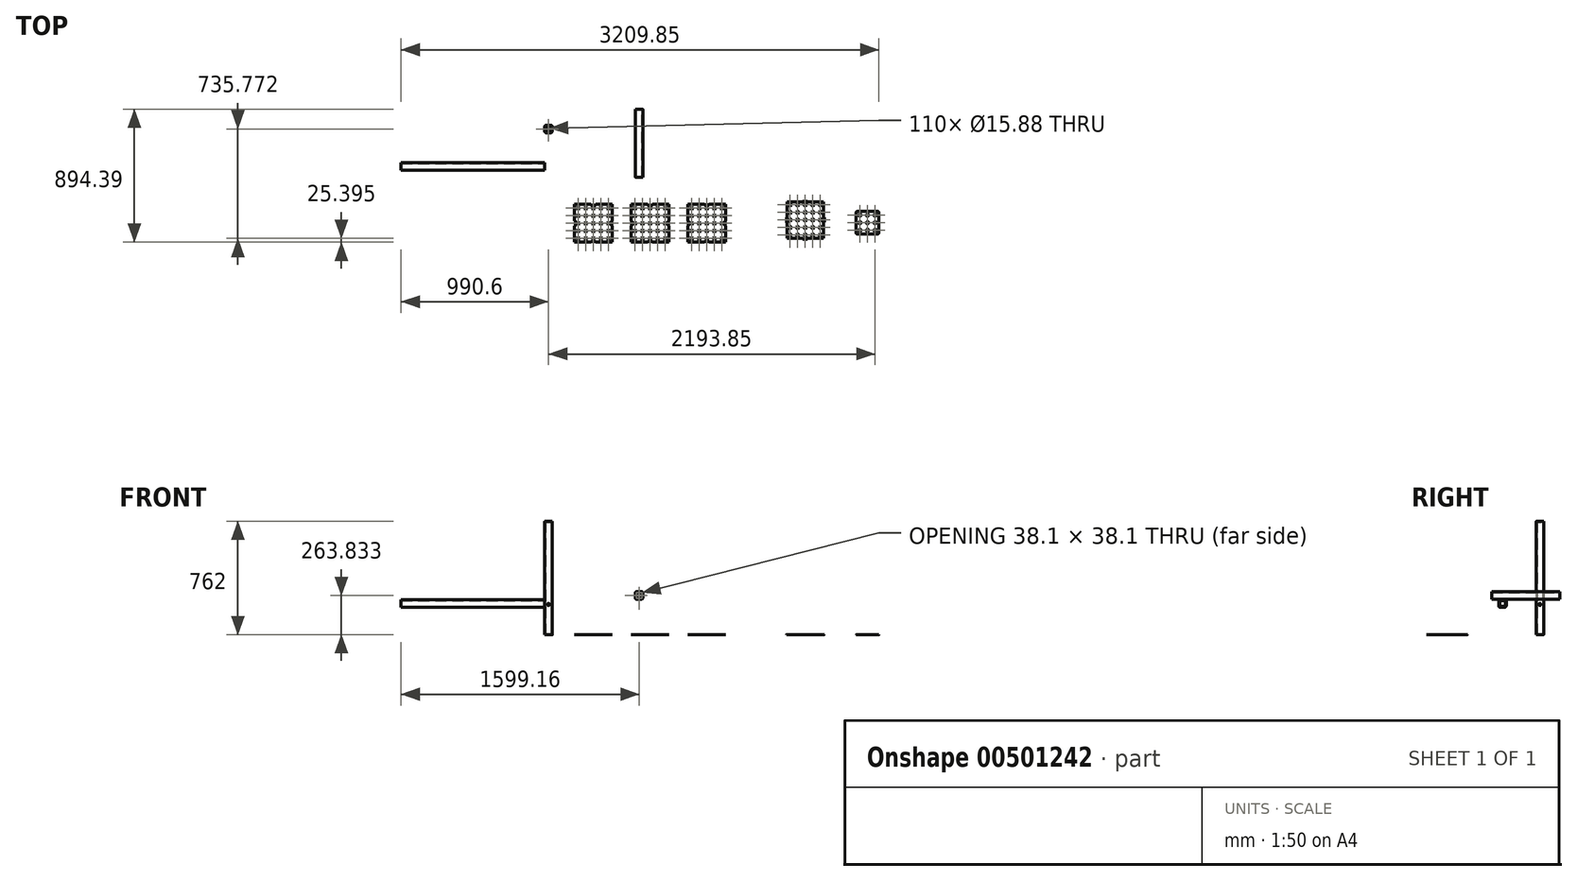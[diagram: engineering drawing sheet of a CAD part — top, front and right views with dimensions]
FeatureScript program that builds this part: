
annotation { "Feature Type Name" : "Feature", "Feature Type Description" : "" }
export const myFeature = defineFeature(function(context is Context, id is Id, definition is map)
    precondition{}
    {
        {
            assignVariable(context, id + "F0", {"name" : "TopPlateThickness", "anyValue" : 0.25});
        }
        {
            assignVariable(context, id + "F1", {"name" : "CornerPlateThickness", "anyValue" : 0.25});
        }
        {
            var Q0;
            Q0=qCreatedBy(makeId("Top.planeOp"),FACE);
            var sketch = newSketch(context, id + "F2", { "sketchPlane" : qUnion([Q0])});
            skLineSegment(sketch, "E0.bottom", {"start": v(-372.68, -640.4) * mm, "end": v(-118.68, -640.4) * mm});
            skLineSegment(sketch, "E0.top", {"start": v(-372.68, -894.4) * mm, "end": v(-118.68, -894.4) * mm});
            skLineSegment(sketch, "E0.left", {"start": v(-372.68, -640.4) * mm, "end": v(-372.68, -894.4) * mm});
            skLineSegment(sketch, "E0.right", {"start": v(-118.68, -640.4) * mm, "end": v(-118.68, -894.4) * mm});
            skLineSegment(sketch, "E1", {"start": v(-372.68, -665.8) * mm, "end": v(-347.28, -665.8) * mm, "construction": true});
            skLineSegment(sketch, "E2", {"start": v(-347.28, -665.8) * mm, "end": v(-347.28, -640.4) * mm, "construction": true});
            skCircle(sketch, "E3", {"center": v(-347.28, -665.8) * mm, "radius": 7.94 * mm});
            skCircle(sketch, "E4.0.1.0", {"center": v(-347.28, -716.6) * mm, "radius": 7.94 * mm});
            skCircle(sketch, "E4.0.2.0", {"center": v(-347.28, -767.4) * mm, "radius": 7.94 * mm});
            skCircle(sketch, "E4.0.3.0", {"center": v(-347.28, -818.2) * mm, "radius": 7.94 * mm});
            skCircle(sketch, "E4.1.0.0", {"center": v(-296.48, -665.8) * mm, "radius": 7.94 * mm});
            skCircle(sketch, "E4.1.1.0", {"center": v(-296.48, -716.6) * mm, "radius": 7.94 * mm});
            skCircle(sketch, "E4.1.2.0", {"center": v(-296.48, -767.4) * mm, "radius": 7.94 * mm});
            skCircle(sketch, "E4.1.3.0", {"center": v(-296.48, -818.2) * mm, "radius": 7.94 * mm});
            skCircle(sketch, "E4.2.0.0", {"center": v(-245.68, -665.8) * mm, "radius": 7.94 * mm});
            skCircle(sketch, "E4.2.1.0", {"center": v(-245.68, -716.6) * mm, "radius": 7.94 * mm});
            skCircle(sketch, "E4.2.2.0", {"center": v(-245.68, -767.4) * mm, "radius": 7.94 * mm});
            skCircle(sketch, "E4.2.3.0", {"center": v(-245.68, -818.2) * mm, "radius": 7.94 * mm});
            skCircle(sketch, "E4.3.0.0", {"center": v(-194.88, -665.8) * mm, "radius": 7.94 * mm});
            skCircle(sketch, "E4.3.1.0", {"center": v(-194.88, -716.6) * mm, "radius": 7.94 * mm});
            skCircle(sketch, "E4.3.2.0", {"center": v(-194.88, -767.4) * mm, "radius": 7.94 * mm});
            skCircle(sketch, "E4.3.3.0", {"center": v(-194.88, -818.2) * mm, "radius": 7.94 * mm});
            skCircle(sketch, "E4.4.0.0", {"center": v(-144.08, -665.8) * mm, "radius": 7.94 * mm});
            skCircle(sketch, "E4.4.1.0", {"center": v(-144.08, -716.6) * mm, "radius": 7.94 * mm});
            skCircle(sketch, "E4.4.2.0", {"center": v(-144.08, -767.4) * mm, "radius": 7.94 * mm});
            skCircle(sketch, "E4.4.3.0", {"center": v(-144.08, -818.2) * mm, "radius": 7.94 * mm});
            skLineSegment(sketch, "E4.direction1", {"start": v(-347.28, -665.8) * mm, "end": v(-296.48, -665.8) * mm, "construction": true});
            skLineSegment(sketch, "E4.direction2", {"start": v(-347.28, -665.8) * mm, "end": v(-347.28, -716.6) * mm, "construction": true});
            skLineSegment(sketch, "E5.MirrorCS", {"start": v(138.85, -74.13) * mm, "end": v(138.95, -80.47) * mm});
            skLineSegment(sketch, "E6", {"start": v(170.72, -73.61) * mm, "end": v(170.82, -79.96) * mm});
            skArc(sketch, "E7", {"start": v(141.8, -73.28) * mm, "mid": v(140, -72.57) * mm, "end": v(138.85, -74.13) * mm});
            skArc(sketch, "E8", {"start": v(141.8, -73.28) * mm, "mid": v(142.39, -73.86) * mm, "end": v(143.18, -74.06) * mm});
            skArc(sketch, "E9.MirrorCS", {"start": v(167.75, -72.87) * mm, "mid": v(169.52, -72.1) * mm, "end": v(170.72, -73.61) * mm});
            skArc(sketch, "E10.MirrorCS", {"start": v(167.75, -72.87) * mm, "mid": v(167.17, -73.46) * mm, "end": v(166.38, -73.68) * mm});
            skLineSegment(sketch, "E11.trimOffspring", {"start": v(166.38, -73.68) * mm, "end": v(143.18, -74.06) * mm});
            skLineSegment(sketch, "E12", {"start": v(138.85, -74.13) * mm, "end": v(143.18, -74.06) * mm, "construction": true});
            skLineSegment(sketch, "E13", {"start": v(166.38, -73.68) * mm, "end": v(170.72, -73.61) * mm, "construction": true});
            skLineSegment(sketch, "E14", {"start": v(154.78, -73.87) * mm, "end": v(154.89, -80.22) * mm, "construction": true});
            skLineSegment(sketch, "E15", {"start": v(138.95, -80.47) * mm, "end": v(154.89, -80.22) * mm, "construction": true});
            skLineSegment(sketch, "E16.MirrorCS", {"start": v(-261.62, -891.22) * mm, "end": v(-261.62, -894.4) * mm});
            skLineSegment(sketch, "E17", {"start": v(-229.74, -891.22) * mm, "end": v(-229.74, -894.4) * mm});
            skArc(sketch, "E18", {"start": v(-258.66, -890.43) * mm, "mid": v(-260.44, -889.69) * mm, "end": v(-261.62, -891.22) * mm});
            skArc(sketch, "E19", {"start": v(-258.66, -890.43) * mm, "mid": v(-258.08, -891) * mm, "end": v(-257.28, -891.22) * mm});
            skArc(sketch, "E20.MirrorCS", {"start": v(-232.7, -890.43) * mm, "mid": v(-230.92, -889.69) * mm, "end": v(-229.74, -891.22) * mm});
            skArc(sketch, "E21.MirrorCS", {"start": v(-232.7, -890.43) * mm, "mid": v(-233.29, -891) * mm, "end": v(-234.08, -891.22) * mm});
            skLineSegment(sketch, "E22.trimOffspring", {"start": v(-234.08, -891.22) * mm, "end": v(-257.28, -891.22) * mm});
            skLineSegment(sketch, "E23", {"start": v(-261.62, -891.22) * mm, "end": v(-257.28, -891.22) * mm, "construction": true});
            skLineSegment(sketch, "E24", {"start": v(-234.08, -891.22) * mm, "end": v(-229.74, -891.22) * mm, "construction": true});
            skLineSegment(sketch, "E25", {"start": v(-245.68, -891.22) * mm, "end": v(-245.68, -894.4) * mm, "construction": true});
            skLineSegment(sketch, "E26", {"start": v(-261.62, -894.4) * mm, "end": v(-245.68, -894.4) * mm, "construction": true});
            skLineSegment(sketch, "E27.MirrorCS", {"start": v(-366.33, -751.46) * mm, "end": v(-372.68, -751.46) * mm});
            skLineSegment(sketch, "E28", {"start": v(-366.33, -783.33) * mm, "end": v(-372.68, -783.33) * mm});
            skArc(sketch, "E29", {"start": v(-365.54, -754.42) * mm, "mid": v(-364.8, -752.63) * mm, "end": v(-366.33, -751.46) * mm});
            skArc(sketch, "E30", {"start": v(-365.54, -754.42) * mm, "mid": v(-366.12, -755) * mm, "end": v(-366.33, -755.8) * mm});
            skArc(sketch, "E31.MirrorCS", {"start": v(-365.54, -780.37) * mm, "mid": v(-364.8, -782.16) * mm, "end": v(-366.33, -783.33) * mm});
            skArc(sketch, "E32.MirrorCS", {"start": v(-365.54, -780.37) * mm, "mid": v(-366.12, -779.79) * mm, "end": v(-366.33, -779) * mm});
            skLineSegment(sketch, "E33.trimOffspring", {"start": v(-366.33, -779) * mm, "end": v(-366.33, -755.8) * mm});
            skLineSegment(sketch, "E34", {"start": v(-366.33, -751.46) * mm, "end": v(-366.33, -755.8) * mm, "construction": true});
            skLineSegment(sketch, "E35", {"start": v(-366.33, -779) * mm, "end": v(-366.33, -783.33) * mm, "construction": true});
            skLineSegment(sketch, "E36", {"start": v(-366.33, -767.4) * mm, "end": v(-372.68, -767.4) * mm, "construction": true});
            skLineSegment(sketch, "E37", {"start": v(-372.68, -751.46) * mm, "end": v(-372.68, -767.4) * mm, "construction": true});
            skCircle(sketch, "E38.0.0.4", {"center": v(-347.28, -869) * mm, "radius": 7.94 * mm});
            skCircle(sketch, "E38.0.1.4", {"center": v(-296.48, -869) * mm, "radius": 7.94 * mm});
            skCircle(sketch, "E38.0.2.4", {"center": v(-245.68, -869) * mm, "radius": 7.94 * mm});
            skCircle(sketch, "E38.0.3.4", {"center": v(-194.88, -869) * mm, "radius": 7.94 * mm});
            skCircle(sketch, "E38.0.4.4", {"center": v(-144.08, -869) * mm, "radius": 7.94 * mm});
            skLineSegment(sketch, "E39.MirrorCS", {"start": v(-121.86, -783.33) * mm, "end": v(-118.68, -783.33) * mm});
            skLineSegment(sketch, "E40", {"start": v(-121.86, -751.46) * mm, "end": v(-118.68, -751.46) * mm});
            skArc(sketch, "E41", {"start": v(-122.65, -780.37) * mm, "mid": v(-123.39, -782.16) * mm, "end": v(-121.86, -783.33) * mm});
            skArc(sketch, "E42", {"start": v(-122.65, -780.37) * mm, "mid": v(-122.07, -779.79) * mm, "end": v(-121.86, -779) * mm});
            skArc(sketch, "E43.MirrorCS", {"start": v(-122.65, -754.42) * mm, "mid": v(-123.39, -752.63) * mm, "end": v(-121.86, -751.46) * mm});
            skArc(sketch, "E44.MirrorCS", {"start": v(-122.65, -754.42) * mm, "mid": v(-122.07, -755) * mm, "end": v(-121.86, -755.8) * mm});
            skLineSegment(sketch, "E45.trimOffspring", {"start": v(-121.86, -755.8) * mm, "end": v(-121.86, -779) * mm});
            skLineSegment(sketch, "E46", {"start": v(-121.86, -783.33) * mm, "end": v(-121.86, -779) * mm, "construction": true});
            skLineSegment(sketch, "E47", {"start": v(-121.86, -755.8) * mm, "end": v(-121.86, -751.46) * mm, "construction": true});
            skLineSegment(sketch, "E48", {"start": v(-121.86, -767.4) * mm, "end": v(-118.68, -767.4) * mm, "construction": true});
            skLineSegment(sketch, "E49", {"start": v(-118.68, -783.33) * mm, "end": v(-118.68, -767.4) * mm, "construction": true});
            skLineSegment(sketch, "E50.MirrorCS", {"start": v(-229.74, -646.74) * mm, "end": v(-229.74, -640.4) * mm});
            skLineSegment(sketch, "E51", {"start": v(-261.62, -646.74) * mm, "end": v(-261.62, -640.4) * mm});
            skArc(sketch, "E52", {"start": v(-232.7, -647.54) * mm, "mid": v(-230.92, -648.28) * mm, "end": v(-229.74, -646.74) * mm});
            skArc(sketch, "E53", {"start": v(-232.7, -647.54) * mm, "mid": v(-233.29, -646.96) * mm, "end": v(-234.08, -646.74) * mm});
            skArc(sketch, "E54.MirrorCS", {"start": v(-258.66, -647.54) * mm, "mid": v(-260.44, -648.28) * mm, "end": v(-261.62, -646.74) * mm});
            skArc(sketch, "E55.MirrorCS", {"start": v(-258.66, -647.54) * mm, "mid": v(-258.08, -646.96) * mm, "end": v(-257.28, -646.74) * mm});
            skLineSegment(sketch, "E56.trimOffspring", {"start": v(-257.28, -646.74) * mm, "end": v(-234.08, -646.74) * mm});
            skLineSegment(sketch, "E57", {"start": v(-229.74, -646.74) * mm, "end": v(-234.08, -646.74) * mm, "construction": true});
            skLineSegment(sketch, "E58", {"start": v(-257.28, -646.74) * mm, "end": v(-261.62, -646.74) * mm, "construction": true});
            skLineSegment(sketch, "E59", {"start": v(-245.68, -646.74) * mm, "end": v(-245.68, -640.4) * mm, "construction": true});
            skLineSegment(sketch, "E60", {"start": v(-229.74, -640.4) * mm, "end": v(-245.68, -640.4) * mm, "construction": true});
            skLineSegment(sketch, "E61.bottom", {"start": v(8.32, -640.4) * mm, "end": v(262.32, -640.4) * mm});
            skLineSegment(sketch, "E61.top", {"start": v(8.32, -894.4) * mm, "end": v(262.32, -894.4) * mm});
            skLineSegment(sketch, "E61.left", {"start": v(8.32, -640.4) * mm, "end": v(8.32, -894.4) * mm});
            skLineSegment(sketch, "E61.right", {"start": v(262.32, -640.4) * mm, "end": v(262.32, -894.4) * mm});
            skLineSegment(sketch, "E62", {"start": v(8.32, -665.8) * mm, "end": v(33.72, -665.8) * mm, "construction": true});
            skLineSegment(sketch, "E63", {"start": v(33.72, -665.8) * mm, "end": v(33.72, -640.4) * mm, "construction": true});
            skCircle(sketch, "E64", {"center": v(33.72, -665.8) * mm, "radius": 7.94 * mm});
            skCircle(sketch, "E65.0.1.0", {"center": v(33.72, -716.6) * mm, "radius": 7.94 * mm});
            skCircle(sketch, "E65.0.2.0", {"center": v(33.72, -767.4) * mm, "radius": 7.94 * mm});
            skCircle(sketch, "E65.0.3.0", {"center": v(33.72, -818.2) * mm, "radius": 7.94 * mm});
            skCircle(sketch, "E65.1.0.0", {"center": v(84.52, -665.8) * mm, "radius": 7.94 * mm});
            skCircle(sketch, "E65.1.1.0", {"center": v(84.52, -716.6) * mm, "radius": 7.94 * mm});
            skCircle(sketch, "E65.1.2.0", {"center": v(84.52, -767.4) * mm, "radius": 7.94 * mm});
            skCircle(sketch, "E65.1.3.0", {"center": v(84.52, -818.2) * mm, "radius": 7.94 * mm});
            skCircle(sketch, "E65.2.0.0", {"center": v(135.32, -665.8) * mm, "radius": 7.94 * mm});
            skCircle(sketch, "E65.2.1.0", {"center": v(135.32, -716.6) * mm, "radius": 7.94 * mm});
            skCircle(sketch, "E65.2.2.0", {"center": v(135.32, -767.4) * mm, "radius": 7.94 * mm});
            skCircle(sketch, "E65.2.3.0", {"center": v(135.32, -818.2) * mm, "radius": 7.94 * mm});
            skCircle(sketch, "E65.3.0.0", {"center": v(186.12, -665.8) * mm, "radius": 7.94 * mm});
            skCircle(sketch, "E65.3.1.0", {"center": v(186.12, -716.6) * mm, "radius": 7.94 * mm});
            skCircle(sketch, "E65.3.2.0", {"center": v(186.12, -767.4) * mm, "radius": 7.94 * mm});
            skCircle(sketch, "E65.3.3.0", {"center": v(186.12, -818.2) * mm, "radius": 7.94 * mm});
            skCircle(sketch, "E65.4.0.0", {"center": v(236.92, -665.8) * mm, "radius": 7.94 * mm});
            skCircle(sketch, "E65.4.1.0", {"center": v(236.92, -716.6) * mm, "radius": 7.94 * mm});
            skCircle(sketch, "E65.4.2.0", {"center": v(236.92, -767.4) * mm, "radius": 7.94 * mm});
            skCircle(sketch, "E65.4.3.0", {"center": v(236.92, -818.2) * mm, "radius": 7.94 * mm});
            skLineSegment(sketch, "E65.direction1", {"start": v(33.72, -665.8) * mm, "end": v(84.52, -665.8) * mm, "construction": true});
            skLineSegment(sketch, "E65.direction2", {"start": v(33.72, -665.8) * mm, "end": v(33.72, -716.6) * mm, "construction": true});
            skLineSegment(sketch, "E66.MirrorCS", {"start": v(119.38, -891.22) * mm, "end": v(119.38, -894.4) * mm});
            skLineSegment(sketch, "E67", {"start": v(151.26, -891.22) * mm, "end": v(151.26, -894.4) * mm});
            skArc(sketch, "E68", {"start": v(122.34, -890.43) * mm, "mid": v(120.56, -889.69) * mm, "end": v(119.38, -891.22) * mm});
            skArc(sketch, "E69", {"start": v(122.34, -890.43) * mm, "mid": v(122.92, -891) * mm, "end": v(123.72, -891.22) * mm});
            skArc(sketch, "E70.MirrorCS", {"start": v(148.3, -890.43) * mm, "mid": v(150.08, -889.69) * mm, "end": v(151.26, -891.22) * mm});
            skArc(sketch, "E71.MirrorCS", {"start": v(148.3, -890.43) * mm, "mid": v(147.71, -891) * mm, "end": v(146.92, -891.22) * mm});
            skLineSegment(sketch, "E72.trimOffspring", {"start": v(146.92, -891.22) * mm, "end": v(123.72, -891.22) * mm});
            skLineSegment(sketch, "E73", {"start": v(119.38, -891.22) * mm, "end": v(123.72, -891.22) * mm, "construction": true});
            skLineSegment(sketch, "E74", {"start": v(146.92, -891.22) * mm, "end": v(151.26, -891.22) * mm, "construction": true});
            skLineSegment(sketch, "E75", {"start": v(135.32, -891.22) * mm, "end": v(135.32, -894.4) * mm, "construction": true});
            skLineSegment(sketch, "E76", {"start": v(119.38, -894.4) * mm, "end": v(135.32, -894.4) * mm, "construction": true});
            skLineSegment(sketch, "E77.MirrorCS", {"start": v(11.5, -751.46) * mm, "end": v(8.32, -751.46) * mm});
            skLineSegment(sketch, "E78", {"start": v(11.5, -783.33) * mm, "end": v(8.32, -783.33) * mm});
            skArc(sketch, "E79", {"start": v(12.29, -754.42) * mm, "mid": v(13.03, -752.63) * mm, "end": v(11.5, -751.46) * mm});
            skArc(sketch, "E80", {"start": v(12.29, -754.42) * mm, "mid": v(11.7, -755) * mm, "end": v(11.5, -755.8) * mm});
            skArc(sketch, "E81.MirrorCS", {"start": v(12.29, -780.37) * mm, "mid": v(13.03, -782.16) * mm, "end": v(11.5, -783.33) * mm});
            skArc(sketch, "E82.MirrorCS", {"start": v(12.29, -780.37) * mm, "mid": v(11.7, -779.79) * mm, "end": v(11.5, -779) * mm});
            skLineSegment(sketch, "E83.trimOffspring", {"start": v(11.5, -779) * mm, "end": v(11.5, -755.8) * mm});
            skLineSegment(sketch, "E84", {"start": v(11.5, -751.46) * mm, "end": v(11.5, -755.8) * mm, "construction": true});
            skLineSegment(sketch, "E85", {"start": v(11.5, -779) * mm, "end": v(11.5, -783.33) * mm, "construction": true});
            skLineSegment(sketch, "E86", {"start": v(11.5, -767.4) * mm, "end": v(8.32, -767.4) * mm, "construction": true});
            skLineSegment(sketch, "E87", {"start": v(8.32, -751.46) * mm, "end": v(8.32, -767.4) * mm, "construction": true});
            skCircle(sketch, "E88.0.0.4", {"center": v(33.72, -869) * mm, "radius": 7.94 * mm});
            skCircle(sketch, "E88.0.1.4", {"center": v(84.52, -869) * mm, "radius": 7.94 * mm});
            skCircle(sketch, "E88.0.2.4", {"center": v(135.32, -869) * mm, "radius": 7.94 * mm});
            skCircle(sketch, "E88.0.3.4", {"center": v(186.12, -869) * mm, "radius": 7.94 * mm});
            skCircle(sketch, "E88.0.4.4", {"center": v(236.92, -869) * mm, "radius": 7.94 * mm});
            skLineSegment(sketch, "E89.MirrorCS", {"start": v(259.14, -783.33) * mm, "end": v(262.32, -783.33) * mm});
            skLineSegment(sketch, "E90", {"start": v(259.14, -751.46) * mm, "end": v(262.32, -751.46) * mm});
            skArc(sketch, "E91", {"start": v(258.35, -780.37) * mm, "mid": v(257.61, -782.16) * mm, "end": v(259.14, -783.33) * mm});
            skArc(sketch, "E92", {"start": v(258.35, -780.37) * mm, "mid": v(258.93, -779.79) * mm, "end": v(259.14, -779) * mm});
            skArc(sketch, "E93.MirrorCS", {"start": v(258.35, -754.42) * mm, "mid": v(257.61, -752.63) * mm, "end": v(259.14, -751.46) * mm});
            skArc(sketch, "E94.MirrorCS", {"start": v(258.35, -754.42) * mm, "mid": v(258.93, -755) * mm, "end": v(259.14, -755.8) * mm});
            skLineSegment(sketch, "E95.trimOffspring", {"start": v(259.14, -755.8) * mm, "end": v(259.14, -779) * mm});
            skLineSegment(sketch, "E96", {"start": v(259.14, -783.33) * mm, "end": v(259.14, -779) * mm, "construction": true});
            skLineSegment(sketch, "E97", {"start": v(259.14, -755.8) * mm, "end": v(259.14, -751.46) * mm, "construction": true});
            skLineSegment(sketch, "E98", {"start": v(259.14, -767.4) * mm, "end": v(262.32, -767.4) * mm, "construction": true});
            skLineSegment(sketch, "E99", {"start": v(262.32, -783.33) * mm, "end": v(262.32, -767.4) * mm, "construction": true});
            skLineSegment(sketch, "E100.MirrorCS", {"start": v(151.26, -646.74) * mm, "end": v(151.26, -640.4) * mm});
            skLineSegment(sketch, "E101", {"start": v(119.38, -646.74) * mm, "end": v(119.38, -640.4) * mm});
            skArc(sketch, "E102", {"start": v(148.3, -647.54) * mm, "mid": v(150.08, -648.28) * mm, "end": v(151.26, -646.74) * mm});
            skArc(sketch, "E103", {"start": v(148.3, -647.54) * mm, "mid": v(147.71, -646.96) * mm, "end": v(146.92, -646.74) * mm});
            skArc(sketch, "E104.MirrorCS", {"start": v(122.34, -647.54) * mm, "mid": v(120.56, -648.28) * mm, "end": v(119.38, -646.74) * mm});
            skArc(sketch, "E105.MirrorCS", {"start": v(122.34, -647.54) * mm, "mid": v(122.92, -646.96) * mm, "end": v(123.72, -646.74) * mm});
            skLineSegment(sketch, "E106.trimOffspring", {"start": v(123.72, -646.74) * mm, "end": v(146.92, -646.74) * mm});
            skLineSegment(sketch, "E107", {"start": v(151.26, -646.74) * mm, "end": v(146.92, -646.74) * mm, "construction": true});
            skLineSegment(sketch, "E108", {"start": v(123.72, -646.74) * mm, "end": v(119.38, -646.74) * mm, "construction": true});
            skLineSegment(sketch, "E109", {"start": v(135.32, -646.74) * mm, "end": v(135.32, -640.4) * mm, "construction": true});
            skLineSegment(sketch, "E110", {"start": v(151.26, -640.4) * mm, "end": v(135.32, -640.4) * mm, "construction": true});
            skLineSegment(sketch, "E111.bottom", {"start": v(389.32, -640.4) * mm, "end": v(643.32, -640.4) * mm});
            skLineSegment(sketch, "E111.top", {"start": v(389.32, -894.4) * mm, "end": v(643.32, -894.4) * mm});
            skLineSegment(sketch, "E111.left", {"start": v(389.32, -640.4) * mm, "end": v(389.32, -894.4) * mm});
            skLineSegment(sketch, "E111.right", {"start": v(643.32, -640.4) * mm, "end": v(643.32, -894.4) * mm});
            skLineSegment(sketch, "E112", {"start": v(389.32, -665.8) * mm, "end": v(414.72, -665.8) * mm, "construction": true});
            skLineSegment(sketch, "E113", {"start": v(414.72, -665.8) * mm, "end": v(414.72, -640.4) * mm, "construction": true});
            skCircle(sketch, "E114", {"center": v(414.72, -665.8) * mm, "radius": 7.94 * mm});
            skCircle(sketch, "E115.0.1.0", {"center": v(414.72, -716.6) * mm, "radius": 7.94 * mm});
            skCircle(sketch, "E115.0.2.0", {"center": v(414.72, -767.4) * mm, "radius": 7.94 * mm});
            skCircle(sketch, "E115.0.3.0", {"center": v(414.72, -818.2) * mm, "radius": 7.94 * mm});
            skCircle(sketch, "E115.1.0.0", {"center": v(465.52, -665.8) * mm, "radius": 7.94 * mm});
            skCircle(sketch, "E115.1.1.0", {"center": v(465.52, -716.6) * mm, "radius": 7.94 * mm});
            skCircle(sketch, "E115.1.2.0", {"center": v(465.52, -767.4) * mm, "radius": 7.94 * mm});
            skCircle(sketch, "E115.1.3.0", {"center": v(465.52, -818.2) * mm, "radius": 7.94 * mm});
            skCircle(sketch, "E115.2.0.0", {"center": v(516.32, -665.8) * mm, "radius": 7.94 * mm});
            skCircle(sketch, "E115.2.1.0", {"center": v(516.32, -716.6) * mm, "radius": 7.94 * mm});
            skCircle(sketch, "E115.2.2.0", {"center": v(516.32, -767.4) * mm, "radius": 7.94 * mm});
            skCircle(sketch, "E115.2.3.0", {"center": v(516.32, -818.2) * mm, "radius": 7.94 * mm});
            skCircle(sketch, "E115.3.0.0", {"center": v(567.12, -665.8) * mm, "radius": 7.94 * mm});
            skCircle(sketch, "E115.3.1.0", {"center": v(567.12, -716.6) * mm, "radius": 7.94 * mm});
            skCircle(sketch, "E115.3.2.0", {"center": v(567.12, -767.4) * mm, "radius": 7.94 * mm});
            skCircle(sketch, "E115.3.3.0", {"center": v(567.12, -818.2) * mm, "radius": 7.94 * mm});
            skCircle(sketch, "E115.4.0.0", {"center": v(617.92, -665.8) * mm, "radius": 7.94 * mm});
            skCircle(sketch, "E115.4.1.0", {"center": v(617.92, -716.6) * mm, "radius": 7.94 * mm});
            skCircle(sketch, "E115.4.2.0", {"center": v(617.92, -767.4) * mm, "radius": 7.94 * mm});
            skCircle(sketch, "E115.4.3.0", {"center": v(617.92, -818.2) * mm, "radius": 7.94 * mm});
            skLineSegment(sketch, "E115.direction1", {"start": v(414.72, -665.8) * mm, "end": v(465.52, -665.8) * mm, "construction": true});
            skLineSegment(sketch, "E115.direction2", {"start": v(414.72, -665.8) * mm, "end": v(414.72, -716.6) * mm, "construction": true});
            skLineSegment(sketch, "E116.MirrorCS", {"start": v(500.38, -891.22) * mm, "end": v(500.38, -894.4) * mm});
            skLineSegment(sketch, "E117", {"start": v(532.26, -891.22) * mm, "end": v(532.26, -894.4) * mm});
            skArc(sketch, "E118", {"start": v(503.34, -890.43) * mm, "mid": v(501.56, -889.69) * mm, "end": v(500.38, -891.22) * mm});
            skArc(sketch, "E119", {"start": v(503.34, -890.43) * mm, "mid": v(503.92, -891) * mm, "end": v(504.72, -891.22) * mm});
            skArc(sketch, "E120.MirrorCS", {"start": v(529.3, -890.43) * mm, "mid": v(531.08, -889.69) * mm, "end": v(532.26, -891.22) * mm});
            skArc(sketch, "E121.MirrorCS", {"start": v(529.3, -890.43) * mm, "mid": v(528.71, -891) * mm, "end": v(527.92, -891.22) * mm});
            skLineSegment(sketch, "E122.trimOffspring", {"start": v(527.92, -891.22) * mm, "end": v(504.72, -891.22) * mm});
            skLineSegment(sketch, "E123", {"start": v(500.38, -891.22) * mm, "end": v(504.72, -891.22) * mm, "construction": true});
            skLineSegment(sketch, "E124", {"start": v(527.92, -891.22) * mm, "end": v(532.26, -891.22) * mm, "construction": true});
            skLineSegment(sketch, "E125", {"start": v(516.32, -891.22) * mm, "end": v(516.32, -894.4) * mm, "construction": true});
            skLineSegment(sketch, "E126", {"start": v(500.38, -894.4) * mm, "end": v(516.32, -894.4) * mm, "construction": true});
            skLineSegment(sketch, "E127.MirrorCS", {"start": v(392.5, -751.46) * mm, "end": v(389.32, -751.46) * mm});
            skLineSegment(sketch, "E128", {"start": v(392.5, -783.33) * mm, "end": v(389.32, -783.33) * mm});
            skArc(sketch, "E129", {"start": v(393.29, -754.42) * mm, "mid": v(394.03, -752.63) * mm, "end": v(392.5, -751.46) * mm});
            skArc(sketch, "E130", {"start": v(393.29, -754.42) * mm, "mid": v(392.7, -755) * mm, "end": v(392.5, -755.8) * mm});
            skArc(sketch, "E131.MirrorCS", {"start": v(393.29, -780.37) * mm, "mid": v(394.03, -782.16) * mm, "end": v(392.5, -783.33) * mm});
            skArc(sketch, "E132.MirrorCS", {"start": v(393.29, -780.37) * mm, "mid": v(392.7, -779.79) * mm, "end": v(392.5, -779) * mm});
            skLineSegment(sketch, "E133.trimOffspring", {"start": v(392.5, -779) * mm, "end": v(392.5, -755.8) * mm});
            skLineSegment(sketch, "E134", {"start": v(392.5, -751.46) * mm, "end": v(392.5, -755.8) * mm, "construction": true});
            skLineSegment(sketch, "E135", {"start": v(392.5, -779) * mm, "end": v(392.5, -783.33) * mm, "construction": true});
            skLineSegment(sketch, "E136", {"start": v(392.5, -767.4) * mm, "end": v(389.32, -767.4) * mm, "construction": true});
            skLineSegment(sketch, "E137", {"start": v(389.32, -751.46) * mm, "end": v(389.32, -767.4) * mm, "construction": true});
            skCircle(sketch, "E138.0.0.4", {"center": v(414.72, -869) * mm, "radius": 7.94 * mm});
            skCircle(sketch, "E138.0.1.4", {"center": v(465.52, -869) * mm, "radius": 7.94 * mm});
            skCircle(sketch, "E138.0.2.4", {"center": v(516.32, -869) * mm, "radius": 7.94 * mm});
            skCircle(sketch, "E138.0.3.4", {"center": v(567.12, -869) * mm, "radius": 7.94 * mm});
            skCircle(sketch, "E138.0.4.4", {"center": v(617.92, -869) * mm, "radius": 7.94 * mm});
            skLineSegment(sketch, "E139.MirrorCS", {"start": v(640.14, -783.33) * mm, "end": v(643.32, -783.33) * mm});
            skLineSegment(sketch, "E140", {"start": v(640.14, -751.46) * mm, "end": v(643.32, -751.46) * mm});
            skArc(sketch, "E141", {"start": v(639.35, -780.37) * mm, "mid": v(638.61, -782.16) * mm, "end": v(640.14, -783.33) * mm});
            skArc(sketch, "E142", {"start": v(639.35, -780.37) * mm, "mid": v(639.93, -779.79) * mm, "end": v(640.14, -779) * mm});
            skArc(sketch, "E143.MirrorCS", {"start": v(639.35, -754.42) * mm, "mid": v(638.61, -752.63) * mm, "end": v(640.14, -751.46) * mm});
            skArc(sketch, "E144.MirrorCS", {"start": v(639.35, -754.42) * mm, "mid": v(639.93, -755) * mm, "end": v(640.14, -755.8) * mm});
            skLineSegment(sketch, "E145.trimOffspring", {"start": v(640.14, -755.8) * mm, "end": v(640.14, -779) * mm});
            skLineSegment(sketch, "E146", {"start": v(640.14, -783.33) * mm, "end": v(640.14, -779) * mm, "construction": true});
            skLineSegment(sketch, "E147", {"start": v(640.14, -755.8) * mm, "end": v(640.14, -751.46) * mm, "construction": true});
            skLineSegment(sketch, "E148", {"start": v(640.14, -767.4) * mm, "end": v(643.32, -767.4) * mm, "construction": true});
            skLineSegment(sketch, "E149", {"start": v(643.32, -783.33) * mm, "end": v(643.32, -767.4) * mm, "construction": true});
            skLineSegment(sketch, "E150.MirrorCS", {"start": v(532.26, -643.57) * mm, "end": v(532.26, -640.4) * mm});
            skLineSegment(sketch, "E151", {"start": v(500.38, -643.57) * mm, "end": v(500.38, -640.4) * mm});
            skArc(sketch, "E152", {"start": v(529.3, -644.36) * mm, "mid": v(531.08, -645.1) * mm, "end": v(532.26, -643.57) * mm});
            skArc(sketch, "E153", {"start": v(529.3, -644.36) * mm, "mid": v(528.71, -643.78) * mm, "end": v(527.92, -643.57) * mm});
            skArc(sketch, "E154.MirrorCS", {"start": v(503.34, -644.36) * mm, "mid": v(501.56, -645.1) * mm, "end": v(500.38, -643.57) * mm});
            skArc(sketch, "E155.MirrorCS", {"start": v(503.34, -644.36) * mm, "mid": v(503.92, -643.78) * mm, "end": v(504.72, -643.57) * mm});
            skLineSegment(sketch, "E156.trimOffspring", {"start": v(504.72, -643.57) * mm, "end": v(527.92, -643.57) * mm});
            skLineSegment(sketch, "E157", {"start": v(532.26, -643.57) * mm, "end": v(527.92, -643.57) * mm, "construction": true});
            skLineSegment(sketch, "E158", {"start": v(504.72, -643.57) * mm, "end": v(500.38, -643.57) * mm, "construction": true});
            skLineSegment(sketch, "E159", {"start": v(516.32, -643.57) * mm, "end": v(516.32, -640.4) * mm, "construction": true});
            skLineSegment(sketch, "E160", {"start": v(532.26, -640.4) * mm, "end": v(516.32, -640.4) * mm, "construction": true});
            skLineSegment(sketch, "E161.bottom", {"start": v(1056.73, -624.33) * mm, "end": v(1158.45, -624.33) * mm});
            skLineSegment(sketch, "E161.top", {"start": v(1056.73, -868.8) * mm, "end": v(1158.45, -868.8) * mm});
            skLineSegment(sketch, "E161.left", {"start": v(1056.73, -624.33) * mm, "end": v(1056.73, -726.06) * mm});
            skLineSegment(sketch, "E161.right", {"start": v(1301.2, -624.33) * mm, "end": v(1301.2, -726.06) * mm});
            skLineSegment(sketch, "E162", {"start": v(1056.73, -643.38) * mm, "end": v(1075.78, -643.38) * mm, "construction": true});
            skLineSegment(sketch, "E163", {"start": v(1075.78, -643.38) * mm, "end": v(1075.78, -624.33) * mm, "construction": true});
            skCircle(sketch, "E164", {"center": v(1075.78, -643.38) * mm, "radius": 7.94 * mm});
            skCircle(sketch, "E165.0.1.0", {"center": v(1075.78, -694.18) * mm, "radius": 7.94 * mm});
            skCircle(sketch, "E165.0.2.0", {"center": v(1075.78, -744.98) * mm, "radius": 7.94 * mm});
            skCircle(sketch, "E165.0.3.0", {"center": v(1075.78, -795.78) * mm, "radius": 7.94 * mm});
            skCircle(sketch, "E165.1.0.0", {"center": v(1126.58, -643.38) * mm, "radius": 7.94 * mm});
            skCircle(sketch, "E165.1.1.0", {"center": v(1126.58, -694.18) * mm, "radius": 7.94 * mm});
            skCircle(sketch, "E165.1.2.0", {"center": v(1126.58, -744.98) * mm, "radius": 7.94 * mm});
            skCircle(sketch, "E165.1.3.0", {"center": v(1126.58, -795.78) * mm, "radius": 7.94 * mm});
            skCircle(sketch, "E165.2.0.0", {"center": v(1177.38, -643.38) * mm, "radius": 7.94 * mm});
            skCircle(sketch, "E165.2.1.0", {"center": v(1177.38, -694.18) * mm, "radius": 7.94 * mm});
            skCircle(sketch, "E165.2.2.0", {"center": v(1177.38, -744.98) * mm, "radius": 7.94 * mm});
            skCircle(sketch, "E165.2.3.0", {"center": v(1177.38, -795.78) * mm, "radius": 7.94 * mm});
            skCircle(sketch, "E165.3.0.0", {"center": v(1228.18, -643.38) * mm, "radius": 7.94 * mm});
            skCircle(sketch, "E165.3.1.0", {"center": v(1228.18, -694.18) * mm, "radius": 7.94 * mm});
            skCircle(sketch, "E165.3.2.0", {"center": v(1228.18, -744.98) * mm, "radius": 7.94 * mm});
            skCircle(sketch, "E165.3.3.0", {"center": v(1228.18, -795.78) * mm, "radius": 7.94 * mm});
            skCircle(sketch, "E165.4.0.0", {"center": v(1278.98, -643.38) * mm, "radius": 7.94 * mm});
            skCircle(sketch, "E165.4.1.0", {"center": v(1278.98, -694.18) * mm, "radius": 7.94 * mm});
            skCircle(sketch, "E165.4.2.0", {"center": v(1278.98, -744.98) * mm, "radius": 7.94 * mm});
            skCircle(sketch, "E165.4.3.0", {"center": v(1278.98, -795.78) * mm, "radius": 7.94 * mm});
            skLineSegment(sketch, "E165.direction1", {"start": v(1075.78, -643.38) * mm, "end": v(1126.58, -643.38) * mm, "construction": true});
            skLineSegment(sketch, "E165.direction2", {"start": v(1075.78, -643.38) * mm, "end": v(1075.78, -694.18) * mm, "construction": true});
            skCircle(sketch, "E166.0.0.4", {"center": v(1075.78, -846.58) * mm, "radius": 7.94 * mm});
            skCircle(sketch, "E166.0.1.4", {"center": v(1126.58, -846.58) * mm, "radius": 7.94 * mm});
            skCircle(sketch, "E166.0.2.4", {"center": v(1177.38, -846.58) * mm, "radius": 7.94 * mm});
            skCircle(sketch, "E166.0.3.4", {"center": v(1228.18, -846.58) * mm, "radius": 7.94 * mm});
            skCircle(sketch, "E166.0.4.4", {"center": v(1278.98, -846.58) * mm, "radius": 7.94 * mm});
            skLineSegment(sketch, "E167.left", {"start": v(137.1, -100.88) * mm, "end": v(137.33, -104.36) * mm});
            skLineSegment(sketch, "E168", {"start": v(138.6, -99.2) * mm, "end": v(145.18, -98.78) * mm});
            skArc(sketch, "E169.filletArc", {"start": v(138.6, -99.2) * mm, "mid": v(137.5, -99.73) * mm, "end": v(137.1, -100.88) * mm});
            skLineSegment(sketch, "E170", {"start": v(148.67, -103.65) * mm, "end": v(153.04, -103.38) * mm});
            skLineSegment(sketch, "E171.MirrorCS", {"start": v(168.54, -98.9) * mm, "end": v(168.76, -102.39) * mm});
            skLineSegment(sketch, "E172.MirrorCS", {"start": v(166.86, -97.42) * mm, "end": v(160.27, -97.83) * mm});
            skArc(sketch, "E173.MirrorCS", {"start": v(166.86, -97.42) * mm, "mid": v(168, -97.8) * mm, "end": v(168.54, -98.9) * mm});
            skArc(sketch, "E174", {"start": v(146.87, -100.26) * mm, "mid": v(146.33, -99.17) * mm, "end": v(145.18, -98.78) * mm});
            skArc(sketch, "E175", {"start": v(146.99, -102.17) * mm, "mid": v(147.52, -103.26) * mm, "end": v(148.67, -103.65) * mm});
            skArc(sketch, "E176", {"start": v(157.42, -103.1) * mm, "mid": v(158.5, -102.57) * mm, "end": v(158.9, -101.42) * mm});
            skArc(sketch, "E177", {"start": v(160.27, -97.83) * mm, "mid": v(159.18, -98.37) * mm, "end": v(158.78, -99.51) * mm});
            skLineSegment(sketch, "E178", {"start": v(157.42, -103.1) * mm, "end": v(153.04, -103.38) * mm});
            skArc(sketch, "E179", {"start": v(134.16, -104.56) * mm, "mid": v(135.84, -106.05) * mm, "end": v(137.33, -104.36) * mm});
            skArc(sketch, "E180", {"start": v(168.76, -102.39) * mm, "mid": v(170.44, -103.87) * mm, "end": v(171.93, -102.19) * mm});
            skLineSegment(sketch, "E181.0", {"start": v(137.33, -104.36) * mm, "end": v(168.76, -102.39) * mm, "construction": true});
            skLineSegment(sketch, "E182.0", {"start": v(145.28, -100.36) * mm, "end": v(160.37, -99.42) * mm, "construction": true});
            skLineSegment(sketch, "E183.0", {"start": v(138.6, -99.2) * mm, "end": v(166.86, -97.42) * mm, "construction": true});
            skLineSegment(sketch, "E184", {"start": v(138.6, -99.2) * mm, "end": v(138.91, -104.26) * mm, "construction": true});
            skLineSegment(sketch, "E185", {"start": v(146.87, -100.26) * mm, "end": v(146.99, -102.17) * mm});
            skLineSegment(sketch, "E186", {"start": v(158.78, -99.51) * mm, "end": v(158.9, -101.42) * mm});
            skLineSegment(sketch, "E187.left", {"start": v(1161.63, -620.84) * mm, "end": v(1161.63, -624.33) * mm});
            skLineSegment(sketch, "E188", {"start": v(1163.22, -619.25) * mm, "end": v(1169.82, -619.25) * mm});
            skArc(sketch, "E189.filletArc", {"start": v(1163.22, -619.25) * mm, "mid": v(1162.1, -619.72) * mm, "end": v(1161.63, -620.84) * mm});
            skLineSegment(sketch, "E190", {"start": v(1173, -624.33) * mm, "end": v(1177.38, -624.33) * mm});
            skLineSegment(sketch, "E191.MirrorCS", {"start": v(1193.12, -620.84) * mm, "end": v(1193.12, -624.33) * mm});
            skLineSegment(sketch, "E192.MirrorCS", {"start": v(1191.54, -619.25) * mm, "end": v(1184.93, -619.25) * mm});
            skArc(sketch, "E193.MirrorCS", {"start": v(1191.54, -619.25) * mm, "mid": v(1192.66, -619.72) * mm, "end": v(1193.12, -620.84) * mm});
            skArc(sketch, "E194", {"start": v(1171.4, -620.84) * mm, "mid": v(1170.94, -619.72) * mm, "end": v(1169.82, -619.25) * mm});
            skArc(sketch, "E195", {"start": v(1171.4, -622.75) * mm, "mid": v(1171.87, -623.87) * mm, "end": v(1173, -624.33) * mm});
            skArc(sketch, "E196", {"start": v(1181.76, -624.33) * mm, "mid": v(1182.88, -623.87) * mm, "end": v(1183.35, -622.75) * mm});
            skArc(sketch, "E197", {"start": v(1184.93, -619.25) * mm, "mid": v(1183.81, -619.72) * mm, "end": v(1183.35, -620.84) * mm});
            skLineSegment(sketch, "E198", {"start": v(1181.76, -624.33) * mm, "end": v(1177.38, -624.33) * mm});
            skArc(sketch, "E199", {"start": v(1158.45, -624.33) * mm, "mid": v(1160.04, -625.92) * mm, "end": v(1161.63, -624.33) * mm});
            skArc(sketch, "E200", {"start": v(1193.12, -624.33) * mm, "mid": v(1194.71, -625.92) * mm, "end": v(1196.3, -624.33) * mm});
            skLineSegment(sketch, "E201.0", {"start": v(1169.82, -620.84) * mm, "end": v(1184.93, -620.84) * mm, "construction": true});
            skLineSegment(sketch, "E202.0", {"start": v(1163.22, -619.25) * mm, "end": v(1191.54, -619.25) * mm, "construction": true});
            skLineSegment(sketch, "E203", {"start": v(1163.22, -619.25) * mm, "end": v(1163.22, -624.33) * mm, "construction": true});
            skLineSegment(sketch, "E204", {"start": v(1171.4, -620.84) * mm, "end": v(1171.4, -622.75) * mm});
            skLineSegment(sketch, "E205", {"start": v(1183.35, -620.84) * mm, "end": v(1183.35, -622.75) * mm});
            skLineSegment(sketch, "E206.left", {"start": v(1304.7, -729.24) * mm, "end": v(1301.2, -729.24) * mm});
            skLineSegment(sketch, "E207", {"start": v(1306.28, -730.82) * mm, "end": v(1306.28, -737.43) * mm});
            skArc(sketch, "E208.filletArc", {"start": v(1306.28, -730.82) * mm, "mid": v(1305.82, -729.7) * mm, "end": v(1304.7, -729.24) * mm});
            skLineSegment(sketch, "E209", {"start": v(1301.2, -740.6) * mm, "end": v(1301.2, -744.98) * mm});
            skLineSegment(sketch, "E210.MirrorCS", {"start": v(1304.7, -760.73) * mm, "end": v(1301.2, -760.73) * mm});
            skLineSegment(sketch, "E211.MirrorCS", {"start": v(1306.28, -759.14) * mm, "end": v(1306.28, -752.54) * mm});
            skArc(sketch, "E212.MirrorCS", {"start": v(1306.28, -759.14) * mm, "mid": v(1305.82, -760.27) * mm, "end": v(1304.7, -760.73) * mm});
            skArc(sketch, "E213", {"start": v(1304.7, -739.02) * mm, "mid": v(1305.82, -738.55) * mm, "end": v(1306.28, -737.43) * mm});
            skArc(sketch, "E214", {"start": v(1302.79, -739.02) * mm, "mid": v(1301.67, -739.48) * mm, "end": v(1301.2, -740.6) * mm});
            skArc(sketch, "E215", {"start": v(1301.2, -749.37) * mm, "mid": v(1301.67, -750.49) * mm, "end": v(1302.79, -750.95) * mm});
            skArc(sketch, "E216", {"start": v(1306.28, -752.54) * mm, "mid": v(1305.82, -751.42) * mm, "end": v(1304.7, -750.95) * mm});
            skLineSegment(sketch, "E217", {"start": v(1301.2, -749.37) * mm, "end": v(1301.2, -744.98) * mm});
            skArc(sketch, "E218", {"start": v(1301.2, -726.06) * mm, "mid": v(1299.61, -727.65) * mm, "end": v(1301.2, -729.24) * mm});
            skArc(sketch, "E219", {"start": v(1301.2, -760.73) * mm, "mid": v(1299.61, -762.32) * mm, "end": v(1301.2, -763.9) * mm});
            skLineSegment(sketch, "E220.0", {"start": v(1304.7, -737.43) * mm, "end": v(1304.7, -752.54) * mm, "construction": true});
            skLineSegment(sketch, "E221.0", {"start": v(1306.28, -730.82) * mm, "end": v(1306.28, -759.14) * mm, "construction": true});
            skLineSegment(sketch, "E222", {"start": v(1306.28, -730.82) * mm, "end": v(1301.2, -730.82) * mm, "construction": true});
            skLineSegment(sketch, "E223", {"start": v(1304.7, -739.02) * mm, "end": v(1302.79, -739.02) * mm});
            skLineSegment(sketch, "E224", {"start": v(1304.7, -750.95) * mm, "end": v(1302.79, -750.95) * mm});
            skLineSegment(sketch, "E225.left", {"start": v(1193.12, -872.3) * mm, "end": v(1193.12, -868.8) * mm});
            skLineSegment(sketch, "E226", {"start": v(1191.54, -873.89) * mm, "end": v(1184.93, -873.89) * mm});
            skArc(sketch, "E227.filletArc", {"start": v(1191.54, -873.89) * mm, "mid": v(1192.66, -873.42) * mm, "end": v(1193.12, -872.3) * mm});
            skLineSegment(sketch, "E228", {"start": v(1181.76, -868.8) * mm, "end": v(1177.38, -868.8) * mm});
            skLineSegment(sketch, "E229.MirrorCS", {"start": v(1161.63, -872.3) * mm, "end": v(1161.63, -868.8) * mm});
            skLineSegment(sketch, "E230.MirrorCS", {"start": v(1163.22, -873.89) * mm, "end": v(1169.82, -873.89) * mm});
            skArc(sketch, "E231.MirrorCS", {"start": v(1163.22, -873.89) * mm, "mid": v(1162.1, -873.42) * mm, "end": v(1161.63, -872.3) * mm});
            skArc(sketch, "E232", {"start": v(1183.35, -872.3) * mm, "mid": v(1183.81, -873.42) * mm, "end": v(1184.93, -873.89) * mm});
            skArc(sketch, "E233", {"start": v(1183.35, -870.4) * mm, "mid": v(1182.88, -869.27) * mm, "end": v(1181.76, -868.8) * mm});
            skArc(sketch, "E234", {"start": v(1173, -868.8) * mm, "mid": v(1171.87, -869.27) * mm, "end": v(1171.4, -870.4) * mm});
            skArc(sketch, "E235", {"start": v(1169.82, -873.89) * mm, "mid": v(1170.94, -873.42) * mm, "end": v(1171.4, -872.3) * mm});
            skLineSegment(sketch, "E236", {"start": v(1173, -868.8) * mm, "end": v(1177.38, -868.8) * mm});
            skArc(sketch, "E237", {"start": v(1196.3, -868.8) * mm, "mid": v(1194.71, -867.22) * mm, "end": v(1193.12, -868.8) * mm});
            skArc(sketch, "E238", {"start": v(1161.63, -868.8) * mm, "mid": v(1160.04, -867.22) * mm, "end": v(1158.45, -868.8) * mm});
            skLineSegment(sketch, "E239.0", {"start": v(1184.93, -872.3) * mm, "end": v(1169.82, -872.3) * mm, "construction": true});
            skLineSegment(sketch, "E240.0", {"start": v(1191.54, -873.89) * mm, "end": v(1163.22, -873.89) * mm, "construction": true});
            skLineSegment(sketch, "E241", {"start": v(1191.54, -873.89) * mm, "end": v(1191.54, -868.8) * mm, "construction": true});
            skLineSegment(sketch, "E242", {"start": v(1183.35, -872.3) * mm, "end": v(1183.35, -870.4) * mm});
            skLineSegment(sketch, "E243", {"start": v(1171.4, -872.3) * mm, "end": v(1171.4, -870.4) * mm});
            skLineSegment(sketch, "E244.left", {"start": v(1053.23, -760.73) * mm, "end": v(1056.73, -760.73) * mm});
            skLineSegment(sketch, "E245", {"start": v(1051.65, -759.14) * mm, "end": v(1051.65, -752.54) * mm});
            skArc(sketch, "E246.filletArc", {"start": v(1051.65, -759.14) * mm, "mid": v(1052.11, -760.27) * mm, "end": v(1053.23, -760.73) * mm});
            skLineSegment(sketch, "E247", {"start": v(1056.73, -749.37) * mm, "end": v(1056.73, -744.98) * mm});
            skLineSegment(sketch, "E248.MirrorCS", {"start": v(1053.23, -729.24) * mm, "end": v(1056.73, -729.24) * mm});
            skLineSegment(sketch, "E249.MirrorCS", {"start": v(1051.65, -730.82) * mm, "end": v(1051.65, -737.43) * mm});
            skArc(sketch, "E250.MirrorCS", {"start": v(1051.65, -730.82) * mm, "mid": v(1052.11, -729.7) * mm, "end": v(1053.23, -729.24) * mm});
            skArc(sketch, "E251", {"start": v(1053.23, -750.95) * mm, "mid": v(1052.11, -751.42) * mm, "end": v(1051.65, -752.54) * mm});
            skArc(sketch, "E252", {"start": v(1055.14, -750.95) * mm, "mid": v(1056.26, -750.49) * mm, "end": v(1056.73, -749.37) * mm});
            skArc(sketch, "E253", {"start": v(1056.73, -740.6) * mm, "mid": v(1056.26, -739.48) * mm, "end": v(1055.14, -739.02) * mm});
            skArc(sketch, "E254", {"start": v(1051.65, -737.43) * mm, "mid": v(1052.11, -738.55) * mm, "end": v(1053.23, -739.02) * mm});
            skLineSegment(sketch, "E255", {"start": v(1056.73, -740.6) * mm, "end": v(1056.73, -744.98) * mm});
            skArc(sketch, "E256", {"start": v(1056.73, -763.9) * mm, "mid": v(1058.31, -762.32) * mm, "end": v(1056.73, -760.73) * mm});
            skArc(sketch, "E257", {"start": v(1056.73, -729.24) * mm, "mid": v(1058.31, -727.65) * mm, "end": v(1056.73, -726.06) * mm});
            skLineSegment(sketch, "E258.0", {"start": v(1056.73, -760.73) * mm, "end": v(1056.73, -729.24) * mm, "construction": true});
            skLineSegment(sketch, "E259.0", {"start": v(1053.23, -752.54) * mm, "end": v(1053.23, -737.43) * mm, "construction": true});
            skLineSegment(sketch, "E260.0", {"start": v(1051.65, -759.14) * mm, "end": v(1051.65, -730.82) * mm, "construction": true});
            skLineSegment(sketch, "E261", {"start": v(1051.65, -759.14) * mm, "end": v(1056.73, -759.14) * mm, "construction": true});
            skLineSegment(sketch, "E262", {"start": v(1053.23, -750.95) * mm, "end": v(1055.14, -750.95) * mm});
            skLineSegment(sketch, "E263", {"start": v(1053.23, -739.02) * mm, "end": v(1055.14, -739.02) * mm});
            skLineSegment(sketch, "E264", {"start": v(1056.73, -744.98) * mm, "end": v(1301.2, -744.98) * mm, "construction": true});
            skLineSegment(sketch, "E265", {"start": v(1177.38, -624.33) * mm, "end": v(1177.38, -868.8) * mm, "construction": true});
            skLineSegment(sketch, "E266.trimOffspring", {"start": v(1196.3, -624.33) * mm, "end": v(1301.2, -624.33) * mm});
            skLineSegment(sketch, "E267.trimOffspring", {"start": v(1301.2, -763.9) * mm, "end": v(1301.2, -868.8) * mm});
            skLineSegment(sketch, "E268.trimOffspring", {"start": v(1056.73, -763.9) * mm, "end": v(1056.73, -868.8) * mm});
            skLineSegment(sketch, "E269.trimOffspring", {"start": v(1196.3, -868.8) * mm, "end": v(1301.2, -868.8) * mm});
            skLineSegment(sketch, "E270", {"start": v(1161.63, -624.33) * mm, "end": v(1193.12, -624.33) * mm, "construction": true});
            skPoint(sketch, "E271.visualSharp", {"position": v(1056.73, -868.8) * mm});
            skLineSegment(sketch, "E271.filletArc", {"start": v(1056.73, -868.8) * mm, "end": v(1056.73, -868.8) * mm});
            skPoint(sketch, "E272.visualSharp", {"position": v(1301.2, -868.8) * mm});
            skLineSegment(sketch, "E272.filletArc", {"start": v(1301.2, -868.8) * mm, "end": v(1301.2, -868.8) * mm});
            skPoint(sketch, "E273.visualSharp", {"position": v(1301.2, -624.33) * mm});
            skLineSegment(sketch, "E273.filletArc", {"start": v(1301.2, -624.33) * mm, "end": v(1301.2, -624.33) * mm});
            skPoint(sketch, "E274.visualSharp", {"position": v(1056.73, -624.33) * mm});
            skLineSegment(sketch, "E274.filletArc", {"start": v(1056.73, -624.33) * mm, "end": v(1056.73, -624.33) * mm});
            skLineSegment(sketch, "E275.bottom", {"start": v(1528.03, -687.21) * mm, "end": v(1664.55, -687.21) * mm});
            skLineSegment(sketch, "E275.top", {"start": v(1528.03, -839.61) * mm, "end": v(1664.55, -839.61) * mm});
            skLineSegment(sketch, "E275.right", {"start": v(1672.49, -695.15) * mm, "end": v(1672.49, -831.67) * mm});
            skLineSegment(sketch, "E276", {"start": v(1520.09, -712.61) * mm, "end": v(1545.49, -712.61) * mm, "construction": true});
            skLineSegment(sketch, "E277", {"start": v(1545.49, -712.61) * mm, "end": v(1545.49, -687.21) * mm, "construction": true});
            skCircle(sketch, "E278", {"center": v(1545.49, -712.61) * mm, "radius": 7.94 * mm});
            skCircle(sketch, "E279.0.1.0", {"center": v(1545.49, -763.41) * mm, "radius": 7.94 * mm});
            skCircle(sketch, "E279.0.2.0", {"center": v(1545.49, -814.21) * mm, "radius": 7.94 * mm});
            skCircle(sketch, "E279.1.0.0", {"center": v(1596.29, -712.61) * mm, "radius": 7.94 * mm});
            skCircle(sketch, "E279.1.1.0", {"center": v(1596.29, -763.41) * mm, "radius": 7.94 * mm});
            skCircle(sketch, "E279.1.2.0", {"center": v(1596.29, -814.21) * mm, "radius": 7.94 * mm});
            skCircle(sketch, "E279.2.0.0", {"center": v(1647.09, -712.61) * mm, "radius": 7.94 * mm});
            skCircle(sketch, "E279.2.1.0", {"center": v(1647.09, -763.41) * mm, "radius": 7.94 * mm});
            skCircle(sketch, "E279.2.2.0", {"center": v(1647.09, -814.21) * mm, "radius": 7.94 * mm});
            skLineSegment(sketch, "E279.direction1", {"start": v(1545.49, -712.61) * mm, "end": v(1596.29, -712.61) * mm, "construction": true});
            skLineSegment(sketch, "E279.direction2", {"start": v(1545.49, -712.61) * mm, "end": v(1545.49, -763.41) * mm, "construction": true});
            skLineSegment(sketch, "E280.trimOffspring", {"start": v(1520.09, -695.15) * mm, "end": v(1520.09, -831.67) * mm});
            skPoint(sketch, "E281.visualSharp", {"position": v(1520.09, -839.61) * mm});
            skArc(sketch, "E281.filletArc", {"start": v(1520.09, -831.67) * mm, "mid": v(1522.41, -837.29) * mm, "end": v(1528.03, -839.61) * mm});
            skPoint(sketch, "E282.visualSharp", {"position": v(1520.09, -687.21) * mm});
            skArc(sketch, "E282.filletArc", {"start": v(1528.03, -687.21) * mm, "mid": v(1522.41, -689.54) * mm, "end": v(1520.09, -695.15) * mm});
            skPoint(sketch, "E283.visualSharp", {"position": v(1672.49, -687.21) * mm});
            skArc(sketch, "E283.filletArc", {"start": v(1672.49, -695.15) * mm, "mid": v(1670.16, -689.54) * mm, "end": v(1664.55, -687.21) * mm});
            skPoint(sketch, "E284.visualSharp", {"position": v(1672.49, -839.61) * mm});
            skArc(sketch, "E284.filletArc", {"start": v(1664.55, -839.61) * mm, "mid": v(1670.16, -837.29) * mm, "end": v(1672.49, -831.67) * mm});
            skSolve(sketch);
        }
        {
            var Q0;
            Q0=makeQuery(id+"F2.imprint","IMPRINT",FACE,{"disambiguationData":[TD([[makeQuery(id+"F2.imprint","IMPRINT",EDGE,{"derivedFrom":sQuery(id+"F2.wireOp",EDGE,"E3")}),-1.0]])]});
            var Q1;
            Q1=makeQuery(id+"F2.imprint","IMPRINT",FACE,{"disambiguationData":[TD([[makeQuery(id+"F2.imprint","IMPRINT",EDGE,{"derivedFrom":sQuery(id+"F2.wireOp",EDGE,"E64")}),-1.0]])]});
            var Q2;
            Q2=makeQuery(id+"F2.imprint","IMPRINT",FACE,{"disambiguationData":[TD([[makeQuery(id+"F2.imprint","IMPRINT",EDGE,{"derivedFrom":sQuery(id+"F2.wireOp",EDGE,"E114")}),-1.0]])]});
            extrude(context, id + "F3", {"entities" : qUnion([Q0, Q1, Q2]), "depth" : (getVariable(context, 'TopPlateThickness')) * mm});
        }
        {
            var Q0;
            Q0=makeQuery(id+"F2.imprint","IMPRINT",FACE,{"disambiguationData":[TD([[makeQuery(id+"F2.imprint","IMPRINT",EDGE,{"derivedFrom":sQuery(id+"F2.wireOp",EDGE,"E164")}),-1.0]])]});
            var Q1;
            Q1=makeQuery(id+"F2.imprint","IMPRINT",FACE,{"disambiguationData":[TD([[makeQuery(id+"F2.imprint","IMPRINT",EDGE,{"derivedFrom":sQuery(id+"F2.wireOp",EDGE,"E275.bottom")}),-1.0]])]});
            extrude(context, id + "F4", {"entities" : qUnion([Q0, Q1]), "depth" : (getVariable(context, 'CornerPlateThickness')) * mm});
        }
        {
            var Q0;
            Q0=qCreatedBy(makeId("Top.planeOp"),FACE);
            var sketch = newSketch(context, id + "F5", { "sketchPlane" : qUnion([Q0])});
            skLineSegment(sketch, "E285.bottom", {"start": v(-562.63, -114.17) * mm, "end": v(-530.88, -114.17) * mm});
            skLineSegment(sketch, "E285.top", {"start": v(-562.63, -152.27) * mm, "end": v(-530.88, -152.27) * mm});
            skLineSegment(sketch, "E285.left", {"start": v(-565.8, -117.35) * mm, "end": v(-565.8, -149.1) * mm});
            skLineSegment(sketch, "E285.right", {"start": v(-527.7, -117.35) * mm, "end": v(-527.7, -149.1) * mm});
            skPoint(sketch, "E286.visualSharp", {"position": v(-565.8, -114.17) * mm});
            skArc(sketch, "E286.filletArc", {"start": v(-562.63, -114.17) * mm, "mid": v(-564.88, -115.1) * mm, "end": v(-565.8, -117.35) * mm});
            skPoint(sketch, "E287.visualSharp", {"position": v(-527.7, -114.17) * mm});
            skArc(sketch, "E287.filletArc", {"start": v(-527.7, -117.35) * mm, "mid": v(-528.64, -115.1) * mm, "end": v(-530.88, -114.17) * mm});
            skPoint(sketch, "E288.visualSharp", {"position": v(-527.7, -152.27) * mm});
            skArc(sketch, "E288.filletArc", {"start": v(-530.88, -152.27) * mm, "mid": v(-528.64, -151.34) * mm, "end": v(-527.7, -149.1) * mm});
            skPoint(sketch, "E289.visualSharp", {"position": v(-565.8, -152.27) * mm});
            skArc(sketch, "E289.filletArc", {"start": v(-565.8, -149.1) * mm, "mid": v(-564.88, -151.34) * mm, "end": v(-562.63, -152.27) * mm});
            skArc(sketch, "E290.0", {"start": v(-572.16, -149.1) * mm, "mid": v(-569.37, -155.83) * mm, "end": v(-562.63, -158.62) * mm});
            skLineSegment(sketch, "E290.1", {"start": v(-572.16, -117.35) * mm, "end": v(-572.16, -149.1) * mm});
            skLineSegment(sketch, "E290.2", {"start": v(-562.63, -158.62) * mm, "end": v(-530.88, -158.62) * mm});
            skArc(sketch, "E290.3", {"start": v(-562.63, -107.82) * mm, "mid": v(-569.37, -110.61) * mm, "end": v(-572.16, -117.35) * mm});
            skArc(sketch, "E290.4", {"start": v(-530.88, -158.62) * mm, "mid": v(-524.15, -155.83) * mm, "end": v(-521.36, -149.1) * mm});
            skLineSegment(sketch, "E290.5", {"start": v(-521.36, -117.35) * mm, "end": v(-521.36, -149.1) * mm});
            skArc(sketch, "E290.6", {"start": v(-521.36, -117.35) * mm, "mid": v(-524.15, -110.61) * mm, "end": v(-530.88, -107.82) * mm});
            skLineSegment(sketch, "E290.7", {"start": v(-562.63, -107.82) * mm, "end": v(-530.88, -107.82) * mm});
            skSolve(sketch);
        }
        {
            var Q0;
            Q0=makeQuery(id+"F5.imprint","IMPRINT",FACE,{"disambiguationData":[TD([[makeQuery(id+"F5.imprint","IMPRINT",EDGE,{"derivedFrom":sQuery(id+"F5.wireOp",EDGE,"E285.bottom")}),1.0]])]});
            extrude(context, id + "F6", {"entities" : qUnion([Q0]), "depth" : 762 * mm});
        }
        {
            var Q0;
            Q0=makeQuery(id+"F6.opExtrude","CAP_FACE",FACE,{"disambiguationData":[OSD([sQuery(id+"F5.wireOp",EDGE,"E285.bottom"),sQuery(id+"F5.wireOp",EDGE,"E285.top"),sQuery(id+"F5.wireOp",EDGE,"E285.left"),sQuery(id+"F5.wireOp",EDGE,"E285.right"),sQuery(id+"F5.wireOp",EDGE,"E286.filletArc"),sQuery(id+"F5.wireOp",EDGE,"E287.filletArc"),sQuery(id+"F5.wireOp",EDGE,"E288.filletArc"),sQuery(id+"F5.wireOp",EDGE,"E289.filletArc"),sQuery(id+"F5.wireOp",EDGE,"E290.0"),sQuery(id+"F5.wireOp",EDGE,"E290.1"),sQuery(id+"F5.wireOp",EDGE,"E290.2"),sQuery(id+"F5.wireOp",EDGE,"E290.3"),sQuery(id+"F5.wireOp",EDGE,"E290.4"),sQuery(id+"F5.wireOp",EDGE,"E290.5"),sQuery(id+"F5.wireOp",EDGE,"E290.6"),sQuery(id+"F5.wireOp",EDGE,"E290.7")])],"isStart":false});
            var sketch = newSketch(context, id + "F7", { "sketchPlane" : qUnion([Q0])});
            skLineSegment(sketch, "E291", {"start": v(-565.8, -149.1) * mm, "end": v(-565.8, -117.35) * mm});
            skLineSegment(sketch, "E292", {"start": v(-562.63, -114.17) * mm, "end": v(-530.88, -114.17) * mm});
            skLineSegment(sketch, "E293", {"start": v(-527.7, -117.35) * mm, "end": v(-527.7, -149.1) * mm});
            skLineSegment(sketch, "E294", {"start": v(-530.88, -152.27) * mm, "end": v(-562.63, -152.27) * mm});
            skArc(sketch, "E295", {"start": v(-562.63, -152.27) * mm, "mid": v(-564.88, -151.34) * mm, "end": v(-565.8, -149.1) * mm});
            skArc(sketch, "E296", {"start": v(-565.8, -117.35) * mm, "mid": v(-564.88, -115.1) * mm, "end": v(-562.63, -114.17) * mm});
            skArc(sketch, "E297", {"start": v(-530.88, -114.17) * mm, "mid": v(-528.64, -115.1) * mm, "end": v(-527.7, -117.35) * mm});
            skArc(sketch, "E298", {"start": v(-527.7, -149.1) * mm, "mid": v(-528.64, -151.34) * mm, "end": v(-530.88, -152.27) * mm});
            skLineSegment(sketch, "E299", {"start": v(-562.63, -117.35) * mm, "end": v(-530.88, -149.1) * mm});
            skCircle(sketch, "E300", {"center": v(-546.76, -133.22) * mm, "radius": 7.94 * mm});
            skSolve(sketch);
        }
        {
            var Q0;
            Q0=makeQuery(id+"F7.imprint","IMPRINT",FACE,{"disambiguationData":[TD([[makeQuery(id+"F7.imprint","IMPRINT",EDGE,{"derivedFrom":sQuery(id+"F7.wireOp",EDGE,"E291")}),1.0]])]});
            extrude(context, id + "F8", {"entities" : qUnion([Q0]), "oppositeDirection" : true, "depth" : 6.35 * mm});
        }
        {
            var Q0;
            Q0=makeQuery(id+"F6.opExtrude","SWEPT_FACE",FACE,{"disambiguationData":[OSD([sQuery(id+"F5.wireOp",EDGE,"E290.2")])]});
            var sketch = newSketch(context, id + "F9", { "sketchPlane" : qUnion([Q0])});
            skLineSegment(sketch, "E301", {"start": v(-546.76, 0) * mm, "end": v(-546.76, 203.2) * mm});
            skCircle(sketch, "E302", {"center": v(-546.76, 203.2) * mm, "radius": 7.94 * mm});
            skSolve(sketch);
        }
        {
            var Q0;
            Q0=makeQuery(id+"F9.imprint","IMPRINT",FACE,{"disambiguationData":[TD([[makeQuery(id+"F9.imprint","IMPRINT",EDGE,{"derivedFrom":sQuery(id+"F9.wireOp",EDGE,"E302")}),1.0]])]});
            extrude(context, id + "F10", {"entities" : qUnion([Q0]), "operationType" : NewBodyOperationType.REMOVE, "oppositeDirection" : true, "depth" : 50.8 * mm});
        }
        {
            var Q0;
            Q0=makeQuery(id+"F6.opExtrude","SWEPT_FACE",FACE,{"disambiguationData":[OSD([sQuery(id+"F5.wireOp",EDGE,"E290.5")])]});
            var sketch = newSketch(context, id + "F11", { "sketchPlane" : qUnion([Q0])});
            skLineSegment(sketch, "E303", {"start": v(-133.22, 0) * mm, "end": v(-133.22, 203.2) * mm});
            skCircle(sketch, "E304", {"center": v(-133.22, 203.2) * mm, "radius": 7.94 * mm});
            skSolve(sketch);
        }
        {
            var Q0;
            Q0=makeQuery(id+"F11.imprint","IMPRINT",FACE,{"disambiguationData":[TD([[makeQuery(id+"F11.imprint","IMPRINT",EDGE,{"derivedFrom":sQuery(id+"F11.wireOp",EDGE,"E304")}),1.0]])]});
            extrude(context, id + "F12", {"entities" : qUnion([Q0]), "operationType" : NewBodyOperationType.REMOVE, "oppositeDirection" : true, "depth" : 50.8 * mm});
        }
        {
            var Q0;
            Q0=makeQuery(id+"F6.opExtrude","SWEPT_FACE",FACE,{"disambiguationData":[OSD([sQuery(id+"F5.wireOp",EDGE,"E290.1")])]});
            var sketch = newSketch(context, id + "F13", { "sketchPlane" : qUnion([Q0])});
            skLineSegment(sketch, "E305.bottom", {"start": v(368.48, 228.53) * mm, "end": v(400.23, 228.53) * mm});
            skLineSegment(sketch, "E305.top", {"start": v(368.48, 190.43) * mm, "end": v(400.23, 190.43) * mm});
            skLineSegment(sketch, "E305.left", {"start": v(365.3, 225.36) * mm, "end": v(365.3, 193.6) * mm});
            skLineSegment(sketch, "E305.right", {"start": v(403.4, 225.36) * mm, "end": v(403.4, 193.6) * mm});
            skPoint(sketch, "E306.visualSharp", {"position": v(365.3, 228.53) * mm});
            skArc(sketch, "E306.filletArc", {"start": v(368.48, 228.53) * mm, "mid": v(366.23, 227.6) * mm, "end": v(365.3, 225.36) * mm});
            skPoint(sketch, "E307.visualSharp", {"position": v(403.4, 228.53) * mm});
            skArc(sketch, "E307.filletArc", {"start": v(403.4, 225.36) * mm, "mid": v(402.47, 227.6) * mm, "end": v(400.23, 228.53) * mm});
            skPoint(sketch, "E308.visualSharp", {"position": v(403.4, 190.43) * mm});
            skArc(sketch, "E308.filletArc", {"start": v(400.23, 190.43) * mm, "mid": v(402.47, 191.36) * mm, "end": v(403.4, 193.6) * mm});
            skPoint(sketch, "E309.visualSharp", {"position": v(365.3, 190.43) * mm});
            skArc(sketch, "E309.filletArc", {"start": v(365.3, 193.6) * mm, "mid": v(366.23, 191.36) * mm, "end": v(368.48, 190.43) * mm});
            skArc(sketch, "E310.0", {"start": v(358.95, 193.6) * mm, "mid": v(361.74, 186.87) * mm, "end": v(368.48, 184.08) * mm});
            skLineSegment(sketch, "E310.1", {"start": v(358.95, 225.36) * mm, "end": v(358.95, 193.6) * mm});
            skLineSegment(sketch, "E310.2", {"start": v(368.48, 184.08) * mm, "end": v(400.23, 184.08) * mm});
            skArc(sketch, "E310.3", {"start": v(368.48, 234.88) * mm, "mid": v(361.74, 232.1) * mm, "end": v(358.95, 225.36) * mm});
            skArc(sketch, "E310.4", {"start": v(400.23, 184.08) * mm, "mid": v(406.96, 186.87) * mm, "end": v(409.75, 193.6) * mm});
            skLineSegment(sketch, "E310.5", {"start": v(409.75, 225.36) * mm, "end": v(409.75, 193.6) * mm});
            skArc(sketch, "E310.6", {"start": v(409.75, 225.36) * mm, "mid": v(406.96, 232.1) * mm, "end": v(400.23, 234.88) * mm});
            skLineSegment(sketch, "E310.7", {"start": v(368.48, 234.88) * mm, "end": v(400.23, 234.88) * mm});
            skSolve(sketch);
        }
        {
            var Q0;
            Q0=qCreatedBy(makeId("Front.planeOp"),FACE);
            var sketch = newSketch(context, id + "F14", { "sketchPlane" : qUnion([Q0])});
            skLineSegment(sketch, "E311.bottom", {"start": v(45.93, 282.88) * mm, "end": v(77.68, 282.88) * mm});
            skLineSegment(sketch, "E311.top", {"start": v(45.93, 244.78) * mm, "end": v(77.68, 244.78) * mm});
            skLineSegment(sketch, "E311.left", {"start": v(42.75, 279.7) * mm, "end": v(42.75, 247.96) * mm});
            skLineSegment(sketch, "E311.right", {"start": v(80.85, 279.7) * mm, "end": v(80.85, 247.96) * mm});
            skPoint(sketch, "E312.visualSharp", {"position": v(42.75, 282.88) * mm});
            skArc(sketch, "E312.filletArc", {"start": v(45.93, 282.88) * mm, "mid": v(43.68, 281.95) * mm, "end": v(42.75, 279.7) * mm});
            skPoint(sketch, "E313.visualSharp", {"position": v(80.85, 282.88) * mm});
            skArc(sketch, "E313.filletArc", {"start": v(80.85, 279.7) * mm, "mid": v(79.92, 281.95) * mm, "end": v(77.68, 282.88) * mm});
            skPoint(sketch, "E314.visualSharp", {"position": v(80.85, 244.78) * mm});
            skArc(sketch, "E314.filletArc", {"start": v(77.68, 244.78) * mm, "mid": v(79.92, 245.71) * mm, "end": v(80.85, 247.96) * mm});
            skPoint(sketch, "E315.visualSharp", {"position": v(42.75, 244.78) * mm});
            skArc(sketch, "E315.filletArc", {"start": v(42.75, 247.96) * mm, "mid": v(43.68, 245.71) * mm, "end": v(45.93, 244.78) * mm});
            skArc(sketch, "E316.0", {"start": v(36.4, 247.96) * mm, "mid": v(39.2, 241.22) * mm, "end": v(45.93, 238.43) * mm});
            skLineSegment(sketch, "E316.1", {"start": v(36.4, 279.7) * mm, "end": v(36.4, 247.96) * mm});
            skLineSegment(sketch, "E316.2", {"start": v(45.93, 238.43) * mm, "end": v(77.68, 238.43) * mm});
            skArc(sketch, "E316.3", {"start": v(45.93, 289.23) * mm, "mid": v(39.2, 286.44) * mm, "end": v(36.4, 279.7) * mm});
            skArc(sketch, "E316.4", {"start": v(77.68, 238.43) * mm, "mid": v(84.41, 241.22) * mm, "end": v(87.2, 247.96) * mm});
            skLineSegment(sketch, "E316.5", {"start": v(87.2, 279.7) * mm, "end": v(87.2, 247.96) * mm});
            skArc(sketch, "E316.6", {"start": v(87.2, 279.7) * mm, "mid": v(84.41, 286.44) * mm, "end": v(77.68, 289.23) * mm});
            skLineSegment(sketch, "E316.7", {"start": v(45.93, 289.23) * mm, "end": v(77.68, 289.23) * mm});
            skSolve(sketch);
        }
        {
            var Q0;
            Q0=makeQuery(id+"F14.imprint","IMPRINT",FACE,{"disambiguationData":[TD([[makeQuery(id+"F14.imprint","IMPRINT",EDGE,{"derivedFrom":sQuery(id+"F14.wireOp",EDGE,"E311.bottom")}),1.0]])]});
            extrude(context, id + "F15", {"entities" : qUnion([Q0]), "depth" : 457.2 * mm});
        }
        {
            var Q0;
            Q0=makeQuery(id+"F13.imprint","IMPRINT",FACE,{"disambiguationData":[TD([[makeQuery(id+"F13.imprint","IMPRINT",EDGE,{"derivedFrom":sQuery(id+"F13.wireOp",EDGE,"E305.bottom")}),1.0]])]});
            extrude(context, id + "F16", {"entities" : qUnion([Q0]), "depth" : 965.2 * mm});
        }
    });
